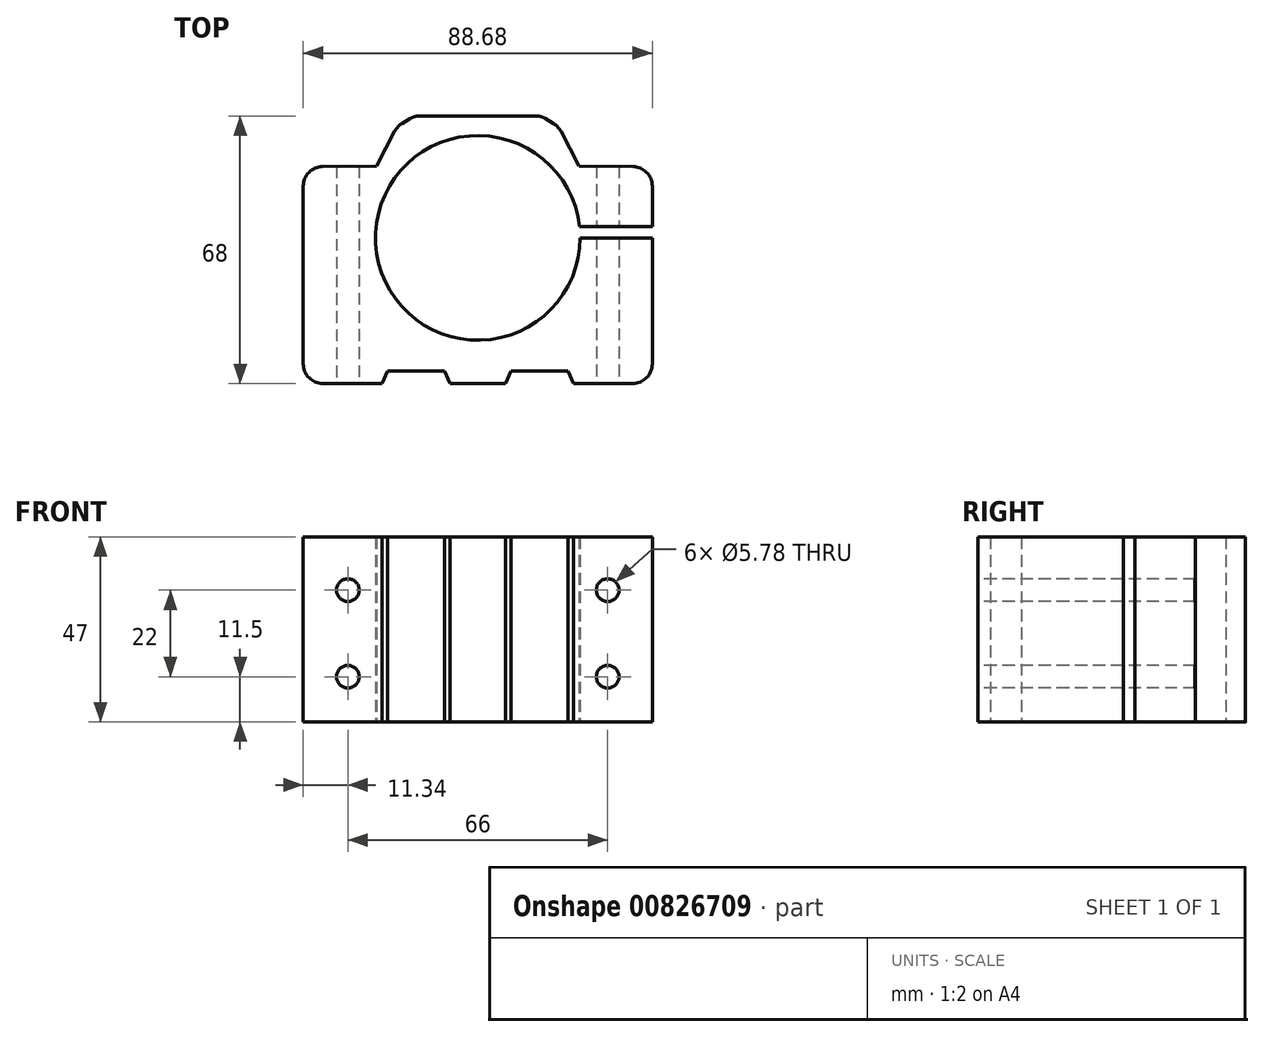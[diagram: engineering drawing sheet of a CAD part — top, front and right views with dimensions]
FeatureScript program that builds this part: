
annotation { "Feature Type Name" : "Feature", "Feature Type Description" : "" }
export const myFeature = defineFeature(function(context is Context, id is Id, definition is map)
    precondition{}
    {
        {
            var Q0;
            Q0=qCreatedBy(makeId("Front.planeOp"),FACE);
            var sketch = newSketch(context, id + "F0", { "sketchPlane" : qUnion([Q0])});
            skLineSegment(sketch, "E0", {"start": v(-67.3, 0) * mm, "end": v(78.37, 0) * mm, "construction": true});
            skLineSegment(sketch, "E1", {"start": v(49.98, 45) * mm, "end": v(-56.63, 45) * mm, "construction": true});
            skLineSegment(sketch, "E2", {"start": v(-78.18, 11.5) * mm, "end": v(77.56, 11.5) * mm, "construction": true});
            skLineSegment(sketch, "E3", {"start": v(-75.16, 33.5) * mm, "end": v(75.87, 33.5) * mm, "construction": true});
            skCircle(sketch, "E4", {"center": v(-33, 33.5) * mm, "radius": 2.89 * mm});
            skLineSegment(sketch, "E5", {"start": v(-111.26, 22.5) * mm, "end": v(83.34, 22.5) * mm, "construction": true});
            skCircle(sketch, "E6.MirrorC", {"center": v(-33, 11.5) * mm, "radius": 2.89 * mm});
            skLineSegment(sketch, "E7", {"start": v(0, 0) * mm, "end": v(0, 70.24) * mm, "construction": true});
            skCircle(sketch, "E8.MirrorC", {"center": v(33, 33.5) * mm, "radius": 2.89 * mm});
            skCircle(sketch, "E9.MirrorC", {"center": v(33, 11.5) * mm, "radius": 2.89 * mm});
            skLineSegment(sketch, "E10.MirrorCS", {"start": v(111.26, 22.5) * mm, "end": v(-83.34, 22.5) * mm, "construction": true});
            skLineSegment(sketch, "E11.MirrorCS", {"start": v(0, 45) * mm, "end": v(0, -25.24) * mm, "construction": true});
            skLineSegment(sketch, "E12", {"start": v(-85.8, 39) * mm, "end": v(79.96, 39) * mm, "construction": true});
            skLineSegment(sketch, "E13", {"start": v(-83.76, 6) * mm, "end": v(79.83, 6) * mm, "construction": true});
            skSolve(sketch);
        }
        {
            var Q0;
            Q0=qCreatedBy(makeId("Top.planeOp"),FACE);
            var sketch = newSketch(context, id + "F1", { "sketchPlane" : qUnion([Q0])});
            skLineSegment(sketch, "E14", {"start": v(0, 44.73) * mm, "end": v(0, -41.53) * mm, "construction": true});
            skLineSegment(sketch, "E15", {"start": v(0, 0) * mm, "end": v(-7, 0) * mm});
            skLineSegment(sketch, "E16", {"start": v(-7, 0) * mm, "end": v(-8.42, 3.2) * mm});
            skLineSegment(sketch, "E17", {"start": v(-8.42, 3.2) * mm, "end": v(-22.92, 3.2) * mm});
            skLineSegment(sketch, "E18", {"start": v(-22.92, 3.2) * mm, "end": v(-24.34, 0) * mm});
            skLineSegment(sketch, "E19", {"start": v(-24.34, 0) * mm, "end": v(-44.34, 0) * mm});
            skLineSegment(sketch, "E20.MirrorCS", {"start": v(0, 0) * mm, "end": v(7, 0) * mm});
            skLineSegment(sketch, "E21.MirrorCS", {"start": v(8.42, 3.2) * mm, "end": v(22.92, 3.2) * mm});
            skLineSegment(sketch, "E22.MirrorCS", {"start": v(22.92, 3.2) * mm, "end": v(24.34, 0) * mm});
            skLineSegment(sketch, "E23.MirrorCS", {"start": v(24.34, 0) * mm, "end": v(44.34, 0) * mm});
            skLineSegment(sketch, "E24.MirrorCS", {"start": v(7, 0) * mm, "end": v(8.42, 3.2) * mm});
            skLineSegment(sketch, "E25", {"start": v(-79.93, 37) * mm, "end": v(69.04, 37) * mm, "construction": true});
            skArc(sketch, "E26", {"start": v(25.85, 39.83) * mm, "mid": v(-25.96, 35.58) * mm, "end": v(26, 37) * mm});
            skLineSegment(sketch, "E27", {"start": v(-44.34, 0) * mm, "end": v(-44.34, 55.07) * mm});
            skLineSegment(sketch, "E28", {"start": v(44.34, 0) * mm, "end": v(44.34, 37) * mm});
            skLineSegment(sketch, "E29", {"start": v(-19.05, 68) * mm, "end": v(19.05, 68) * mm});
            skLineSegment(sketch, "E30", {"start": v(44.34, 39.83) * mm, "end": v(25.85, 39.83) * mm});
            skLineSegment(sketch, "E31", {"start": v(44.34, 37) * mm, "end": v(26, 37) * mm});
            skLineSegment(sketch, "E32.trimOffspring", {"start": v(44.34, 39.83) * mm, "end": v(44.34, 55.07) * mm});
            skLineSegment(sketch, "E33", {"start": v(-19.05, 68) * mm, "end": v(-25.76, 55.25) * mm});
            skLineSegment(sketch, "E34", {"start": v(-44.34, 55.07) * mm, "end": v(-25.76, 55.25) * mm});
            skLineSegment(sketch, "E35.MirrorCS", {"start": v(19.05, 68) * mm, "end": v(25.76, 55.25) * mm});
            skLineSegment(sketch, "E36", {"start": v(25.76, 55.25) * mm, "end": v(44.34, 55.07) * mm});
            skSolve(sketch);
        }
        {
            var Q0;
            Q0 = qSketchRegion(id + "F1", true);
            extrude(context, id + "F2", {"entities" : qUnion([Q0]), "depth" : 47 * mm, "offsetDistance" : 25 * mm});
        }
        {
            var Q0;
            Q0 = qSketchRegion(id + "F0", true);
            extrude(context, id + "F3", {"entities" : qUnion([Q0]), "operationType" : NewBodyOperationType.REMOVE, "oppositeDirection" : true, "depth" : 69 * mm, "offsetDistance" : 25 * mm});
        }
        {
            var Q0;
            Q0=makeQuery(id+"F2.opExtrude","SWEPT_EDGE",EDGE,{"disambiguationData":[OSD([sQuery(id+"F1.wireOp",EDGE,"E27"),sQuery(id+"F1.wireOp",EDGE,"E34")])]});
            var Q1;
            Q1=makeQuery(id+"F2.opExtrude","SWEPT_EDGE",EDGE,{"disambiguationData":[OSD([sQuery(id+"F1.wireOp",EDGE,"E32.trimOffspring"),sQuery(id+"F1.wireOp",EDGE,"E36")])]});
            fillet(context, id + "F4", {"entities" : qUnion([Q0, Q1]), "tangentPropagation" : true, "radius" : 5 * mm, "defaultsChanged" : false, "vertexSettings" : [], "allowEdgeOverflow" : false});
        }
        {
            var Q0;
            Q0=makeQuery(id+"F2.opExtrude","SWEPT_EDGE",EDGE,{"disambiguationData":[OSD([sQuery(id+"F1.wireOp",EDGE,"E29"),sQuery(id+"F1.wireOp",EDGE,"E35.MirrorCS")])]});
            var Q1;
            Q1=makeQuery(id+"F2.opExtrude","SWEPT_EDGE",EDGE,{"disambiguationData":[OSD([sQuery(id+"F1.wireOp",EDGE,"E29"),sQuery(id+"F1.wireOp",EDGE,"E33")])]});
            chamfer(context, id + "F5", {"entities" : qUnion([Q0, Q1]), "width" : 5 * mm, "tangentPropagation" : true});
        }
        {
            var Q0;
            {var subQ0=sQuery(id+"F1.wireOp",EDGE,"E35.MirrorCS");Q0=makeQuery(id+"F5.opChamfer","BLEND_EDGE",EDGE,{"blendedFrom":[makeQuery(id+"F2.opExtrude","SWEPT_EDGE",EDGE,{"disambiguationData":[OSD([sQuery(id+"F1.wireOp",EDGE,"E29"),subQ0])]}),makeQuery(id+"F2.opExtrude","SWEPT_FACE",FACE,{"disambiguationData":[OSD([subQ0])]})],"blendedInto":[makeQuery(id+"F2.opExtrude","SWEPT_FACE",FACE,{"disambiguationData":[OSD([subQ0])]})]});}
            var Q1;
            {var subQ0=sQuery(id+"F1.wireOp",EDGE,"E29");Q1=makeQuery(id+"F5.opChamfer","BLEND_EDGE",EDGE,{"blendedFrom":[makeQuery(id+"F2.opExtrude","SWEPT_EDGE",EDGE,{"disambiguationData":[OSD([subQ0,sQuery(id+"F1.wireOp",EDGE,"E35.MirrorCS")])]}),makeQuery(id+"F2.opExtrude","SWEPT_FACE",FACE,{"disambiguationData":[OSD([subQ0])]})],"blendedInto":[makeQuery(id+"F2.opExtrude","SWEPT_FACE",FACE,{"disambiguationData":[OSD([subQ0])]})]});}
            var Q2;
            {var subQ0=sQuery(id+"F1.wireOp",EDGE,"E29");Q2=makeQuery(id+"F5.opChamfer","BLEND_EDGE",EDGE,{"blendedFrom":[makeQuery(id+"F2.opExtrude","SWEPT_EDGE",EDGE,{"disambiguationData":[OSD([subQ0,sQuery(id+"F1.wireOp",EDGE,"E33")])]}),makeQuery(id+"F2.opExtrude","SWEPT_FACE",FACE,{"disambiguationData":[OSD([subQ0])]})],"blendedInto":[makeQuery(id+"F2.opExtrude","SWEPT_FACE",FACE,{"disambiguationData":[OSD([subQ0])]})]});}
            var Q3;
            {var subQ0=sQuery(id+"F1.wireOp",EDGE,"E33");Q3=makeQuery(id+"F5.opChamfer","BLEND_EDGE",EDGE,{"blendedFrom":[makeQuery(id+"F2.opExtrude","SWEPT_EDGE",EDGE,{"disambiguationData":[OSD([sQuery(id+"F1.wireOp",EDGE,"E29"),subQ0])]}),makeQuery(id+"F2.opExtrude","SWEPT_FACE",FACE,{"disambiguationData":[OSD([subQ0])]})],"blendedInto":[makeQuery(id+"F2.opExtrude","SWEPT_FACE",FACE,{"disambiguationData":[OSD([subQ0])]})]});}
            var Q4;
            Q4=makeQuery(id+"F2.opExtrude","SWEPT_EDGE",EDGE,{"disambiguationData":[OSD([sQuery(id+"F1.wireOp",EDGE,"E23.MirrorCS"),sQuery(id+"F1.wireOp",EDGE,"E28")])]});
            var Q5;
            Q5=makeQuery(id+"F2.opExtrude","SWEPT_EDGE",EDGE,{"disambiguationData":[OSD([sQuery(id+"F1.wireOp",EDGE,"E19"),sQuery(id+"F1.wireOp",EDGE,"E27")])]});
            fillet(context, id + "F6", {"entities" : qUnion([Q0, Q1, Q2, Q3, Q4, Q5]), "tangentPropagation" : true, "radius" : 5 * mm, "defaultsChanged" : false, "vertexSettings" : [], "allowEdgeOverflow" : false});
        }
    });
